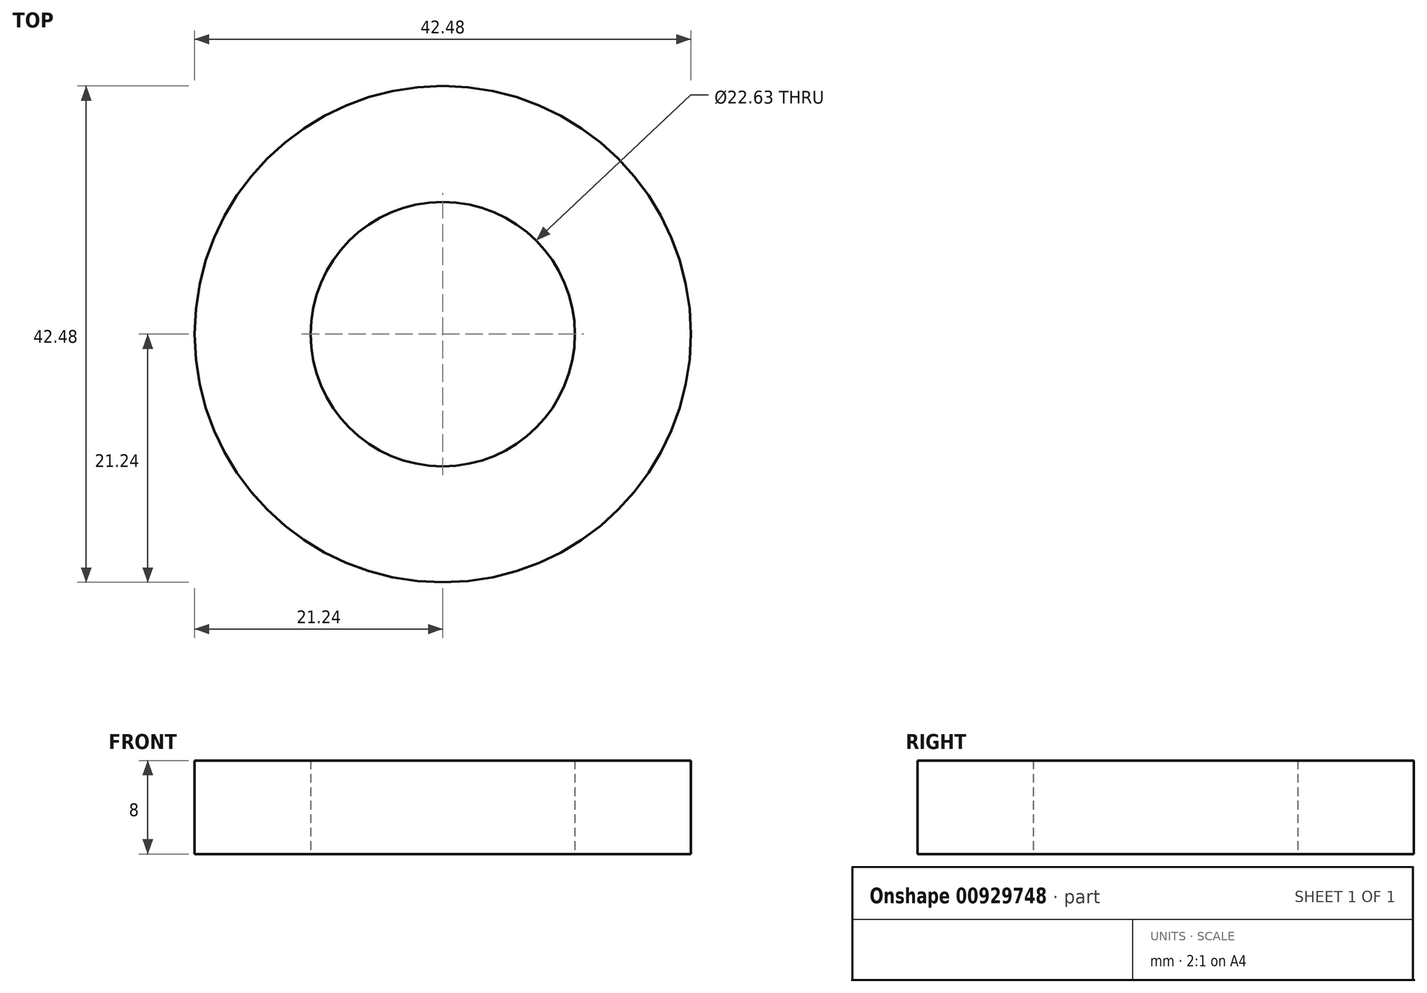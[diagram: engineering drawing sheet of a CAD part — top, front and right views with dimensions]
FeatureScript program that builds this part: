
annotation { "Feature Type Name" : "Feature", "Feature Type Description" : "" }
export const myFeature = defineFeature(function(context is Context, id is Id, definition is map)
    precondition{}
    {
        {
            var Q0;
            Q0=qCreatedBy(makeId("Top.planeOp"),FACE);
            var sketch = newSketch(context, id + "F0", { "sketchPlane" : qUnion([Q0])});
            skCircle(sketch, "E0", {"center": v(34.28, 0) * mm, "radius": 13.04 * mm});
            skCircle(sketch, "E1", {"center": v(0, 0) * mm, "radius": 21.24 * mm});
            skCircle(sketch, "E2", {"center": v(38.49, 12.34) * mm, "radius": 11.7 * mm});
            skCircle(sketch, "E3", {"center": v(0, 0) * mm, "radius": 11.31 * mm});
            skSolve(sketch);
        }
        {
            var Q0;
            Q0=makeQuery(id+"F0.imprint","IMPRINT",FACE,{"disambiguationData":[TD([[makeQuery(id+"F0.imprint","IMPRINT",EDGE,{"derivedFrom":sQuery(id+"F0.wireOp",EDGE,"E1")}),1.0]])]});
            extrude(context, id + "F1", {"entities" : qUnion([Q0]), "endBound" : BoundingType.SYMMETRIC, "depth" : 8 * mm, "offsetDistance" : 25.4 * mm});
        }
    });
